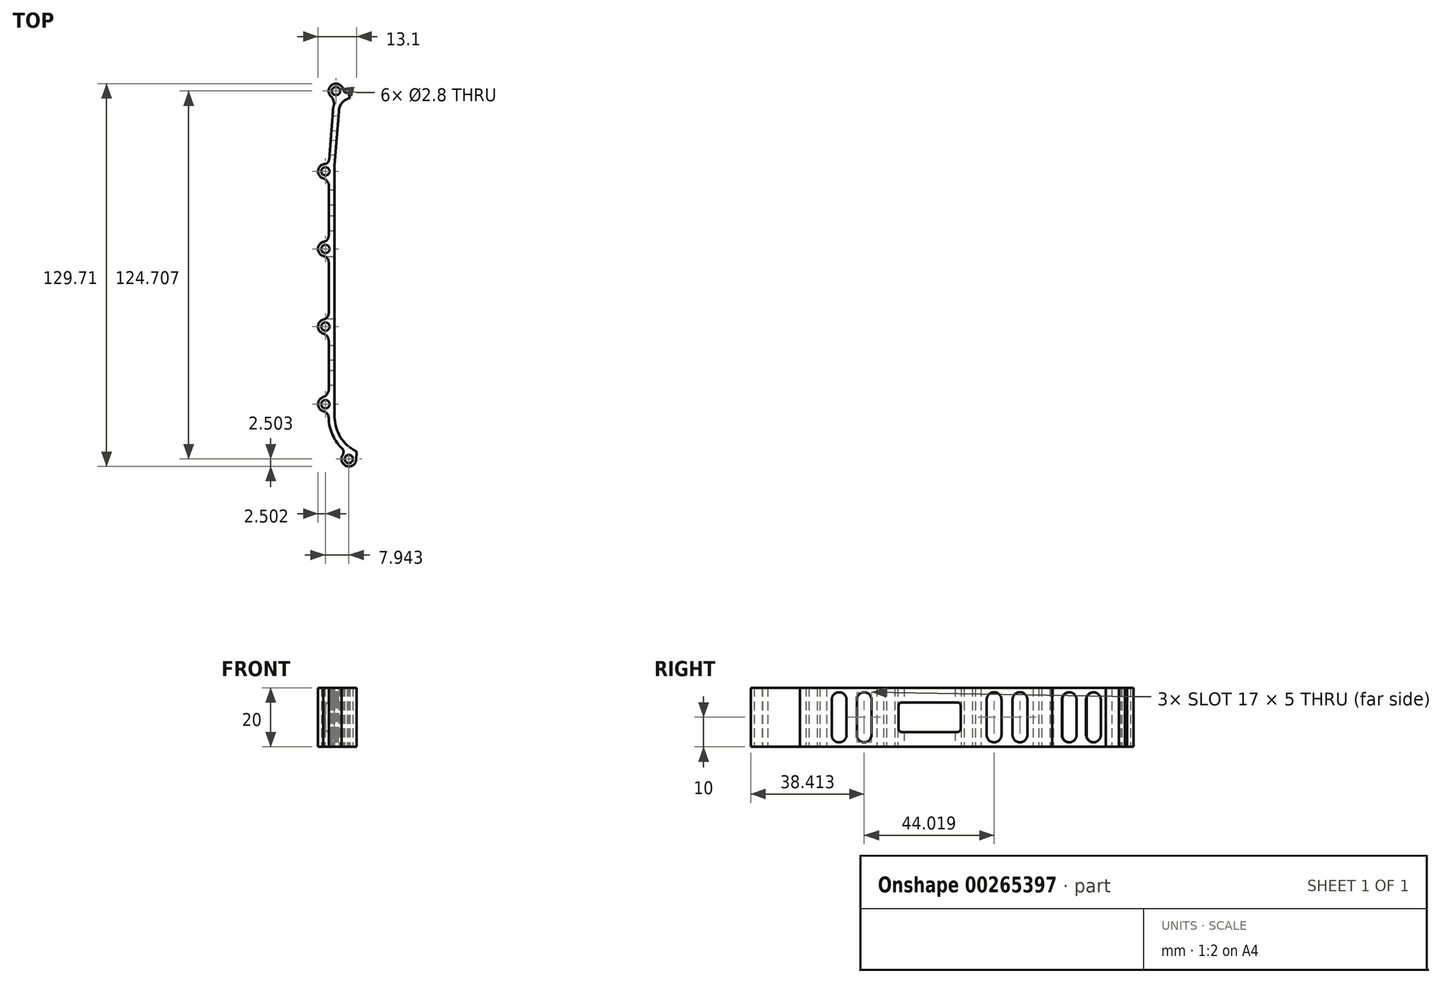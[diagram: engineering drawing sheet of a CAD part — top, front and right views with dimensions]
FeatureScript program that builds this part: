
annotation { "Feature Type Name" : "Feature", "Feature Type Description" : "" }
export const myFeature = defineFeature(function(context is Context, id is Id, definition is map)
    precondition{}
    {
        {
            var Q0;
            Q0=qCreatedBy(makeId("Top.planeOp"),FACE);
            var sketch = newSketch(context, id + "F0", { "sketchPlane" : qUnion([Q0])});
            skCircle(sketch, "E0", {"center": v(112.93, 54.5) * mm, "radius": 1.4 * mm});
            skCircle(sketch, "E1", {"center": v(109.35, 27.28) * mm, "radius": 1.4 * mm});
            skCircle(sketch, "E2", {"center": v(109.35, 0.98) * mm, "radius": 1.4 * mm});
            skCircle(sketch, "E3", {"center": v(109.35, -25.32) * mm, "radius": 1.4 * mm});
            skCircle(sketch, "E4", {"center": v(109.35, -51.62) * mm, "radius": 1.4 * mm});
            skCircle(sketch, "E5", {"center": v(117.3, -70.2) * mm, "radius": 1.4 * mm});
            skArc(sketch, "E6", {"start": v(112.46, -56.1) * mm, "mid": v(114.5, -62.86) * mm, "end": v(119.77, -67.56) * mm});
            skLineSegment(sketch, "E7", {"start": v(112.46, -56.1) * mm, "end": v(112.46, -42.51) * mm});
            skLineSegment(sketch, "E8", {"start": v(112.46, -42.51) * mm, "end": v(112.45, -22.94) * mm});
            skLineSegment(sketch, "E9", {"start": v(112.45, -22.94) * mm, "end": v(112.45, 29.48) * mm});
            skArc(sketch, "E10", {"start": v(117.58, 52.06) * mm, "mid": v(114.93, 50.48) * mm, "end": v(113.89, 47.58) * mm});
            skArc(sketch, "E11", {"start": v(109.2, 29.77) * mm, "mid": v(106.87, 27.55) * mm, "end": v(108.66, 24.87) * mm});
            skArc(sketch, "E12", {"start": v(115.4, 54.86) * mm, "mid": v(111.75, 56.7) * mm, "end": v(111.27, 52.63) * mm});
            skArc(sketch, "E13", {"start": v(108.9, 3.44) * mm, "mid": v(106.85, 0.98) * mm, "end": v(108.9, -1.48) * mm});
            skArc(sketch, "E14", {"start": v(108.88, -22.87) * mm, "mid": v(106.85, -25.25) * mm, "end": v(108.75, -27.75) * mm});
            skArc(sketch, "E15", {"start": v(108.45, -49.3) * mm, "mid": v(106.85, -51.72) * mm, "end": v(108.64, -54.02) * mm});
            skArc(sketch, "E16", {"start": v(115.2, -68.85) * mm, "mid": v(116.51, -72.58) * mm, "end": v(119.79, -70.36) * mm});
            skLineSegment(sketch, "E17", {"start": v(119.95, -67.87) * mm, "end": v(119.79, -70.36) * mm});
            skArc(sketch, "E18.0", {"start": v(110.46, -56.13) * mm, "mid": v(111.78, -62.05) * mm, "end": v(115.34, -66.95) * mm});
            skLineSegment(sketch, "E19", {"start": v(110.46, -47.03) * mm, "end": v(110.46, -30.05) * mm});
            skLineSegment(sketch, "E20.trimOffspring", {"start": v(110.46, 5.34) * mm, "end": v(110.46, 22.88) * mm});
            skLineSegment(sketch, "E21.trimOffspring", {"start": v(110.46, -20.79) * mm, "end": v(110.46, -3.47) * mm});
            skLineSegment(sketch, "E22", {"start": v(112.45, 29.48) * mm, "end": v(113.89, 47.58) * mm});
            skLineSegment(sketch, "E23.0", {"start": v(110.59, 31.23) * mm, "end": v(111.89, 47.66) * mm});
            skArc(sketch, "E24.0", {"start": v(117.2, 54.02) * mm, "mid": v(116.96, 53.97) * mm, "end": v(116.72, 53.9) * mm});
            skArc(sketch, "E25.trimOffspring", {"start": v(112.22, 49.65) * mm, "mid": v(111.98, 48.67) * mm, "end": v(111.89, 47.66) * mm});
            skLineSegment(sketch, "E26", {"start": v(117.58, 52.06) * mm, "end": v(117.2, 54.02) * mm});
            skArc(sketch, "E27", {"start": v(115.36, 55.09) * mm, "mid": v(116, 54.09) * mm, "end": v(117.2, 54.02) * mm});
            skArc(sketch, "E28", {"start": v(112.22, 49.65) * mm, "mid": v(112.04, 51.37) * mm, "end": v(111.08, 52.82) * mm});
            skArc(sketch, "E29", {"start": v(109.07, 29.76) * mm, "mid": v(110.1, 30.22) * mm, "end": v(110.59, 31.24) * mm});
            skArc(sketch, "E30", {"start": v(110.46, 22.88) * mm, "mid": v(109.77, 24.16) * mm, "end": v(108.53, 24.92) * mm});
            skArc(sketch, "E31", {"start": v(108.71, 3.4) * mm, "mid": v(110.01, 4.17) * mm, "end": v(110.46, 5.61) * mm});
            skArc(sketch, "E32", {"start": v(110.46, -3.57) * mm, "mid": v(109.98, -2.18) * mm, "end": v(108.72, -1.44) * mm});
            skArc(sketch, "E33", {"start": v(108.65, -22.92) * mm, "mid": v(109.93, -22.18) * mm, "end": v(110.46, -20.79) * mm});
            skArc(sketch, "E34", {"start": v(110.46, -30.15) * mm, "mid": v(109.95, -28.6) * mm, "end": v(108.58, -27.7) * mm});
            skArc(sketch, "E35", {"start": v(108.45, -49.3) * mm, "mid": v(109.75, -48.43) * mm, "end": v(110.46, -47.03) * mm});
            skArc(sketch, "E36", {"start": v(110.46, -56.13) * mm, "mid": v(109.94, -54.74) * mm, "end": v(108.64, -54.02) * mm});
            skPoint(sketch, "E37.orphan", {"position": v(110.46, -49.38) * mm});
            skPoint(sketch, "E38.end.orphan", {"position": v(110.46, -53.86) * mm});
            skArc(sketch, "E39", {"start": v(115.14, -68.93) * mm, "mid": v(115.49, -67.97) * mm, "end": v(115.34, -66.95) * mm});
            skPoint(sketch, "E40.visualSharp", {"position": v(119.96, -67.65) * mm});
            skArc(sketch, "E40.filletArc", {"start": v(119.95, -67.87) * mm, "mid": v(119.9, -67.69) * mm, "end": v(119.77, -67.56) * mm});
            skSolve(sketch);
        }
        {
            var Q0;
            Q0 = qSketchRegion(id + "F0", true);
            extrude(context, id + "F1", {"entities" : qUnion([Q0]), "depth" : 20 * mm});
        }
        {
            var Q0;
            Q0=makeQuery(id+"F1.opExtrude","SWEPT_FACE",FACE,{"disambiguationData":[OSD([sQuery(id+"F0.wireOp",EDGE,"E21.trimOffspring")])]});
            var sketch = newSketch(context, id + "F2", { "sketchPlane" : qUnion([Q0])});
            skLineSegment(sketch, "E41", {"start": v(12.13, 20) * mm, "end": v(12.13, 0) * mm, "construction": true});
            skLineSegment(sketch, "E42", {"start": v(3.47, 10) * mm, "end": v(20.79, 10) * mm, "construction": true});
            skLineSegment(sketch, "E43.bottom", {"start": v(22.63, 15) * mm, "end": v(1.63, 15) * mm});
            skLineSegment(sketch, "E43.top", {"start": v(22.63, 5) * mm, "end": v(1.63, 5) * mm});
            skLineSegment(sketch, "E43.left", {"start": v(22.63, 15) * mm, "end": v(22.63, 5) * mm});
            skLineSegment(sketch, "E43.right", {"start": v(1.63, 15) * mm, "end": v(1.63, 5) * mm});
            skPoint(sketch, "E43.middle", {"position": v(12.13, 10) * mm});
            skLineSegment(sketch, "E44.0", {"start": v(-5.34, 20) * mm, "end": v(-22.88, 20) * mm, "construction": true});
            skLineSegment(sketch, "E44.1", {"start": v(-5.34, 0) * mm, "end": v(-22.88, 0) * mm, "construction": true});
            skLineSegment(sketch, "E45", {"start": v(-14.1, 20) * mm, "end": v(-14.1, 0) * mm, "construction": true});
            skLineSegment(sketch, "E46.0", {"start": v(-22.88, 20) * mm, "end": v(-22.88, 0) * mm, "construction": true});
            skLineSegment(sketch, "E46.1", {"start": v(-5.34, 20) * mm, "end": v(-5.34, 0) * mm, "construction": true});
            skLineSegment(sketch, "E47", {"start": v(-22.88, 10) * mm, "end": v(-14.1, 10) * mm, "construction": true});
            skPoint(sketch, "E48.orphan", {"position": v(-5.34, 10) * mm});
            skLineSegment(sketch, "E49.bottom", {"start": v(-16, 16) * mm, "end": v(-21, 16) * mm});
            skLineSegment(sketch, "E49.top", {"start": v(-16, 4) * mm, "end": v(-21, 4) * mm});
            skLineSegment(sketch, "E49.left", {"start": v(-16, 16) * mm, "end": v(-16, 4) * mm});
            skLineSegment(sketch, "E49.right", {"start": v(-21, 16) * mm, "end": v(-21, 4) * mm});
            skPoint(sketch, "E49.middle", {"position": v(-18.5, 10) * mm});
            skArc(sketch, "E50", {"start": v(-16, 16) * mm, "mid": v(-18.5, 18.5) * mm, "end": v(-21, 16) * mm});
            skArc(sketch, "E51", {"start": v(-21, 4) * mm, "mid": v(-18.5, 1.5) * mm, "end": v(-16, 4) * mm});
            skArc(sketch, "E52.MirrorCS", {"start": v(-12.22, 16) * mm, "mid": v(-9.72, 18.5) * mm, "end": v(-7.22, 16) * mm});
            skLineSegment(sketch, "E53.MirrorCS", {"start": v(-7.22, 16) * mm, "end": v(-7.22, 4) * mm});
            skLineSegment(sketch, "E54.MirrorCS", {"start": v(-12.22, 4) * mm, "end": v(-7.22, 4) * mm});
            skLineSegment(sketch, "E55.MirrorCS", {"start": v(-12.22, 16) * mm, "end": v(-12.22, 4) * mm});
            skLineSegment(sketch, "E56.MirrorCS", {"start": v(-12.22, 16) * mm, "end": v(-7.22, 16) * mm});
            skPoint(sketch, "E57.MirrorP", {"position": v(-9.72, 10) * mm});
            skArc(sketch, "E58.MirrorCS", {"start": v(-7.22, 4) * mm, "mid": v(-9.72, 1.5) * mm, "end": v(-12.22, 4) * mm});
            skSolve(sketch);
        }
        {
            var Q0;
            Q0 = qSketchRegion(id + "F2", true);
            extrude(context, id + "F3", {"entities" : qUnion([Q0]), "operationType" : NewBodyOperationType.REMOVE, "endBound" : BoundingType.SYMMETRIC, "depth" : 25 * mm, "offsetDistance" : 25 * mm});
        }
        {
            var Q0;
            Q0=makeQuery(id+"F3.boolean.opBoolean","COPY",EDGE,{"derivedFrom":makeQuery(id+"F3.opExtrude","SWEPT_EDGE",EDGE,{"disambiguationData":[OSD([sQuery(id+"F2.wireOp",EDGE,"E43.top"),sQuery(id+"F2.wireOp",EDGE,"E43.left")])]})});
            var Q1;
            Q1=makeQuery(id+"F3.boolean.opBoolean","COPY",EDGE,{"derivedFrom":makeQuery(id+"F3.opExtrude","SWEPT_EDGE",EDGE,{"disambiguationData":[OSD([sQuery(id+"F2.wireOp",EDGE,"E43.top"),sQuery(id+"F2.wireOp",EDGE,"E43.right")])]})});
            var Q2;
            Q2=makeQuery(id+"F3.boolean.opBoolean","COPY",EDGE,{"derivedFrom":makeQuery(id+"F3.opExtrude","SWEPT_EDGE",EDGE,{"disambiguationData":[OSD([sQuery(id+"F2.wireOp",EDGE,"E43.bottom"),sQuery(id+"F2.wireOp",EDGE,"E43.right")])]})});
            var Q3;
            Q3=makeQuery(id+"F3.boolean.opBoolean","COPY",EDGE,{"derivedFrom":makeQuery(id+"F3.opExtrude","SWEPT_EDGE",EDGE,{"disambiguationData":[OSD([sQuery(id+"F2.wireOp",EDGE,"E43.bottom"),sQuery(id+"F2.wireOp",EDGE,"E43.left")])]})});
            fillet(context, id + "F4", {"entities" : qUnion([Q0, Q1, Q2, Q3]), "radius" : 1 * mm, "tangentPropagation" : true, "allowEdgeOverflow" : false});
        }
        {
            var Q0;
            Q0=makeQuery(id+"F1.opExtrude","SWEPT_FACE",FACE,{"disambiguationData":[OSD([sQuery(id+"F0.wireOp",EDGE,"E23.0")])]});
            var sketch = newSketch(context, id + "F5", { "sketchPlane" : qUnion([Q0])});
            skLineSegment(sketch, "E59", {"start": v(-48.1, 20) * mm, "end": v(-48.1, 0) * mm, "construction": true});
            skLineSegment(sketch, "E60", {"start": v(-56.34, 10) * mm, "end": v(-48.1, 10) * mm, "construction": true});
            skLineSegment(sketch, "E61", {"start": v(-52.22, 10) * mm, "end": v(-52.22, 20) * mm, "construction": true});
            skLineSegment(sketch, "E62.bottom", {"start": v(-49.72, 16) * mm, "end": v(-54.72, 16) * mm});
            skLineSegment(sketch, "E62.top", {"start": v(-49.72, 4) * mm, "end": v(-54.72, 4) * mm});
            skLineSegment(sketch, "E62.left", {"start": v(-49.72, 16) * mm, "end": v(-49.72, 4) * mm});
            skLineSegment(sketch, "E62.right", {"start": v(-54.72, 16) * mm, "end": v(-54.72, 4) * mm});
            skPoint(sketch, "E62.middle", {"position": v(-52.22, 10) * mm});
            skArc(sketch, "E63", {"start": v(-49.72, 16) * mm, "mid": v(-52.22, 18.5) * mm, "end": v(-54.72, 16) * mm});
            skArc(sketch, "E64", {"start": v(-54.72, 4) * mm, "mid": v(-52.22, 1.5) * mm, "end": v(-49.72, 4) * mm});
            skLineSegment(sketch, "E65.MirrorCS", {"start": v(-46.48, 16) * mm, "end": v(-41.48, 16) * mm});
            skLineSegment(sketch, "E66.MirrorCS", {"start": v(-46.48, 4) * mm, "end": v(-41.48, 4) * mm});
            skLineSegment(sketch, "E67.MirrorCS", {"start": v(-41.48, 16) * mm, "end": v(-41.48, 4) * mm});
            skLineSegment(sketch, "E68.MirrorCS", {"start": v(-46.48, 16) * mm, "end": v(-46.48, 4) * mm});
            skPoint(sketch, "E69.MirrorP", {"position": v(-43.98, 10) * mm});
            skArc(sketch, "E70.MirrorCS", {"start": v(-46.48, 16) * mm, "mid": v(-43.98, 18.5) * mm, "end": v(-41.48, 16) * mm});
            skArc(sketch, "E71.MirrorCS", {"start": v(-41.48, 4) * mm, "mid": v(-43.98, 1.5) * mm, "end": v(-46.48, 4) * mm});
            skSolve(sketch);
        }
        {
            var Q0;
            Q0 = qSketchRegion(id + "F5", true);
            extrude(context, id + "F6", {"entities" : qUnion([Q0]), "operationType" : NewBodyOperationType.REMOVE, "oppositeDirection" : true, "depth" : 25 * mm, "offsetDistance" : 25 * mm});
        }
        {
            var Q0;
            Q0=makeQuery(id+"F1.opExtrude","SWEPT_FACE",FACE,{"disambiguationData":[OSD([sQuery(id+"F0.wireOp",EDGE,"E19")])]});
            var sketch = newSketch(context, id + "F7", { "sketchPlane" : qUnion([Q0])});
            skLineSegment(sketch, "E72", {"start": v(38.54, 20) * mm, "end": v(38.54, 0) * mm, "construction": true});
            skLineSegment(sketch, "E73", {"start": v(38.54, 10) * mm, "end": v(30.05, 10) * mm, "construction": true});
            skLineSegment(sketch, "E74", {"start": v(34.3, 10) * mm, "end": v(34.3, 20) * mm, "construction": true});
            skLineSegment(sketch, "E75.bottom", {"start": v(36.8, 16) * mm, "end": v(31.8, 16) * mm});
            skLineSegment(sketch, "E75.top", {"start": v(36.8, 4) * mm, "end": v(31.8, 4) * mm});
            skLineSegment(sketch, "E75.left", {"start": v(36.8, 16) * mm, "end": v(36.8, 4) * mm});
            skLineSegment(sketch, "E75.right", {"start": v(31.8, 16) * mm, "end": v(31.8, 4) * mm});
            skPoint(sketch, "E75.middle", {"position": v(34.3, 10) * mm});
            skArc(sketch, "E76", {"start": v(36.8, 16) * mm, "mid": v(34.3, 18.5) * mm, "end": v(31.8, 16) * mm});
            skArc(sketch, "E77", {"start": v(31.8, 4) * mm, "mid": v(34.3, 1.5) * mm, "end": v(36.8, 4) * mm});
            skLineSegment(sketch, "E78.MirrorCS", {"start": v(40.29, 16) * mm, "end": v(45.29, 16) * mm});
            skLineSegment(sketch, "E79.MirrorCS", {"start": v(40.29, 4) * mm, "end": v(45.29, 4) * mm});
            skLineSegment(sketch, "E80.MirrorCS", {"start": v(45.29, 16) * mm, "end": v(45.29, 4) * mm});
            skLineSegment(sketch, "E81.MirrorCS", {"start": v(40.29, 16) * mm, "end": v(40.29, 4) * mm});
            skArc(sketch, "E82.MirrorCS", {"start": v(40.29, 16) * mm, "mid": v(42.79, 18.5) * mm, "end": v(45.29, 16) * mm});
            skArc(sketch, "E83.MirrorCS", {"start": v(45.29, 4) * mm, "mid": v(42.79, 1.5) * mm, "end": v(40.29, 4) * mm});
            skSolve(sketch);
        }
        {
            var Q0;
            Q0 = qSketchRegion(id + "F7", true);
            extrude(context, id + "F8", {"entities" : qUnion([Q0]), "operationType" : NewBodyOperationType.REMOVE, "oppositeDirection" : true, "depth" : 25 * mm, "offsetDistance" : 25 * mm});
        }
    });
